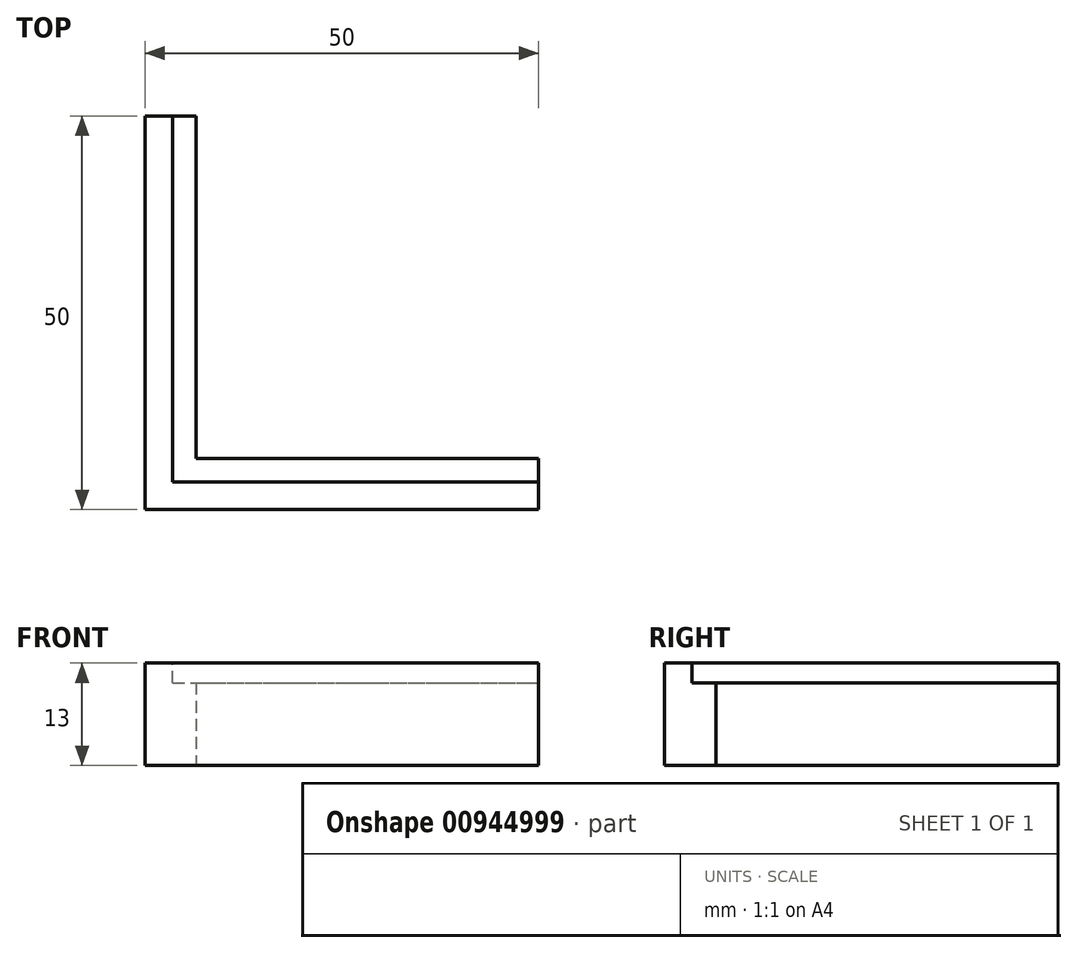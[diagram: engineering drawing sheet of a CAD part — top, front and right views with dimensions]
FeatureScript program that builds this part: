
annotation { "Feature Type Name" : "Feature", "Feature Type Description" : "" }
export const myFeature = defineFeature(function(context is Context, id is Id, definition is map)
    precondition{}
    {
        {
            var Q0;
            Q0=qCreatedBy(makeId("Top.planeOp"),FACE);
            var sketch = newSketch(context, id + "F0", { "sketchPlane" : qUnion([Q0])});
            skLineSegment(sketch, "E0", {"start": v(0, 0) * mm, "end": v(0, 50) * mm});
            skLineSegment(sketch, "E1", {"start": v(0, 50) * mm, "end": v(6.5, 50) * mm});
            skLineSegment(sketch, "E2", {"start": v(6.5, 50) * mm, "end": v(6.5, 6.5) * mm});
            skLineSegment(sketch, "E3", {"start": v(6.5, 6.5) * mm, "end": v(50, 6.5) * mm});
            skLineSegment(sketch, "E4", {"start": v(50, 6.5) * mm, "end": v(50, 0) * mm});
            skLineSegment(sketch, "E5", {"start": v(50, 0) * mm, "end": v(0, 0) * mm});
            skSolve(sketch);
        }
        {
            var Q0;
            Q0=makeQuery(id+"F0.imprint","IMPRINT",FACE,{"disambiguationData":[TD([[makeQuery(id+"F0.imprint","IMPRINT",EDGE,{"derivedFrom":sQuery(id+"F0.wireOp",EDGE,"E0")}),-1.0]])]});
            extrude(context, id + "F1", {"entities" : qUnion([Q0]), "depth" : 13 * mm, "offsetDistance" : 25 * mm});
        }
        {
            var Q0;
            Q0=makeQuery(id+"F1.opExtrude","CAP_FACE",FACE,{"disambiguationData":[OSD([sQuery(id+"F0.wireOp",EDGE,"E0"),sQuery(id+"F0.wireOp",EDGE,"E1"),sQuery(id+"F0.wireOp",EDGE,"E2"),sQuery(id+"F0.wireOp",EDGE,"E3"),sQuery(id+"F0.wireOp",EDGE,"E4"),sQuery(id+"F0.wireOp",EDGE,"E5")])],"isStart":false});
            var sketch = newSketch(context, id + "F2", { "sketchPlane" : qUnion([Q0])});
            skLineSegment(sketch, "E6", {"start": v(6.5, 50) * mm, "end": v(3.5, 50) * mm});
            skLineSegment(sketch, "E7", {"start": v(3.5, 50) * mm, "end": v(3.5, 3.5) * mm});
            skLineSegment(sketch, "E8", {"start": v(3.5, 3.5) * mm, "end": v(50, 3.5) * mm});
            skLineSegment(sketch, "E9", {"start": v(50, 3.5) * mm, "end": v(50, 6.5) * mm});
            skLineSegment(sketch, "E10", {"start": v(50, 6.5) * mm, "end": v(6.5, 6.5) * mm});
            skLineSegment(sketch, "E11", {"start": v(6.5, 6.5) * mm, "end": v(6.5, 50) * mm});
            skSolve(sketch);
        }
        {
            var Q0;
            Q0 = qSketchRegion(id + "F2", true);
            extrude(context, id + "F3", {"entities" : qUnion([Q0]), "operationType" : NewBodyOperationType.REMOVE, "oppositeDirection" : true, "depth" : 2.5 * mm, "offsetDistance" : 25 * mm});
        }
    });
